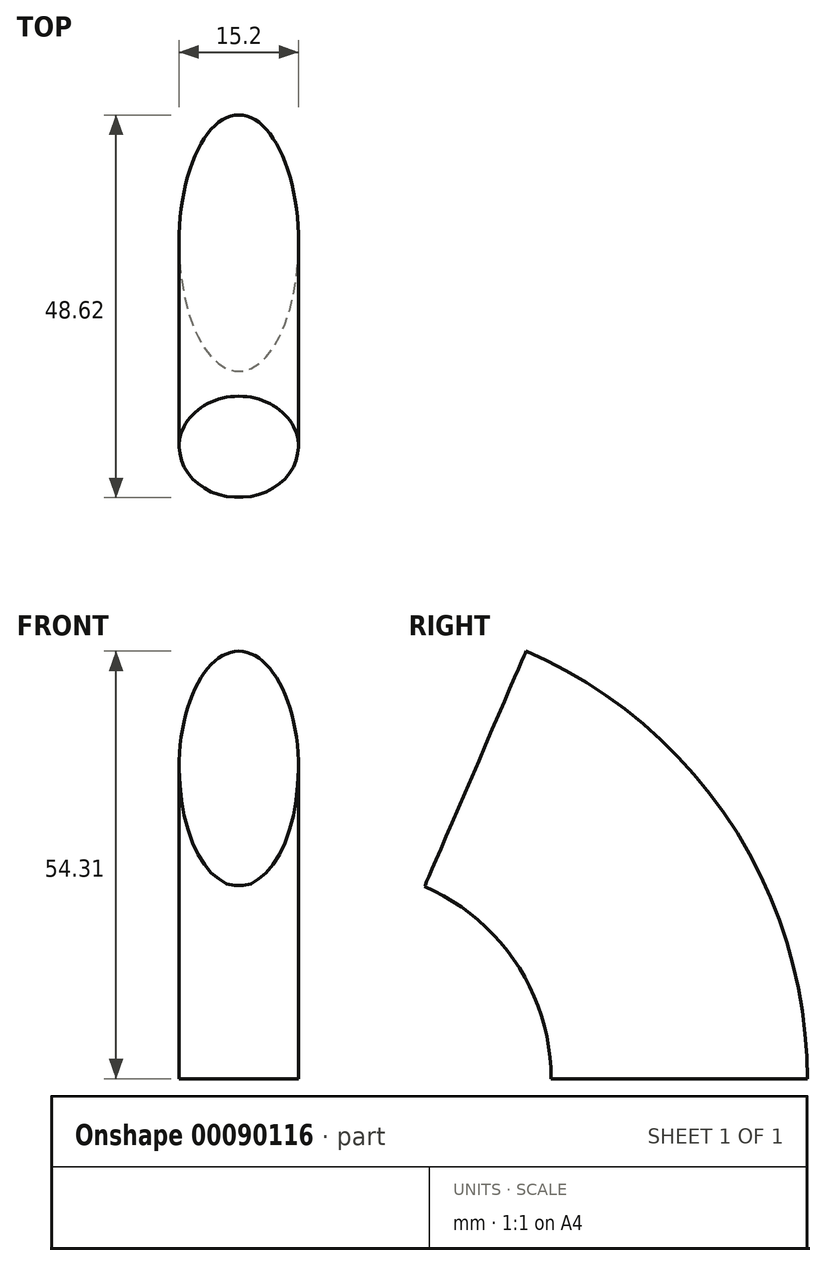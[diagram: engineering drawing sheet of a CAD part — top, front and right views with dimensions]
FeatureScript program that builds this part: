
annotation { "Feature Type Name" : "Feature", "Feature Type Description" : "" }
export const myFeature = defineFeature(function(context is Context, id is Id, definition is map)
    precondition{}
    {
        {
            var Q0;
            Q0=qCreatedBy(makeId("Top.planeOp"),FACE);
            var sketch = newSketch(context, id + "F0", { "sketchPlane" : qUnion([Q0])});
            skEllipse(sketch, "E0", {"center": v(0, 0) * mm, "majorRadius": 16.28 * mm, "minorRadius": 7.6 * mm, "majorAxis": v(0, 1)});
            skSolve(sketch);
        }
        {
            var Q0;
            Q0=qCreatedBy(makeId("Right.planeOp"),FACE);
            var sketch = newSketch(context, id + "F1", { "sketchPlane" : qUnion([Q0])});
            skArc(sketch, "E1", {"start": v(0, 0) * mm, "mid": v(-7.05, 23.56) * mm, "end": v(-25.9, 39.36) * mm});
            skSolve(sketch);
        }
        {
            var Q0;
            Q0=makeQuery(id+"F0.imprint","IMPRINT",FACE,{"disambiguationData":[TD([[makeQuery(id+"F0.imprint","IMPRINT",EDGE,{"derivedFrom":sQuery(id+"F0.wireOp",EDGE,"E0")}),1.0]])]});
            var Q1;
            Q1=sQuery(id+"F1.wireOp",EDGE,"E1");
            sweep(context, id + "F2", {"profiles" : qUnion([Q0]), "path" : qUnion([Q1])});
        }
    });
